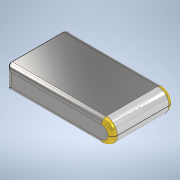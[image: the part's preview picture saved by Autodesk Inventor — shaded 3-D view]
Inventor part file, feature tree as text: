
AUTODESK INVENTOR PART (.ipt)
format: ipt  version: 2022 (Build 260153000, 153)  size: 170,496 bytes
history: native  units: in
note: dims shown in document units (in); Inventor stores cm internally (conversion verified against a paired STEP export)
features: fillet x3, extrude x1, sketch x1
ambient origin geometry x8: Origin, YZ Plane, XZ Plane, XY Plane, X Axis, Y Axis, Z Axis, Center Point
bodies: Solid1 (feature_tree)
feature tree (5):
  extrude  "Extrusion1"  Depth=0.8661in
  fillet  "Fillet1"  Radius=0.9961in
  fillet  "Fillet2"  Radius=0.498in
  fillet  "Fillet3"  Radius=0.3669in
  sketch  "Sketch1"  dims[d0=1.7323in d2=0.8661in d3=0.9961in d4=0.498in d5=0.3669in d6=0.0in d7=0.1811in d8=0.0197in d9=0.0787in d10=0.0in]
